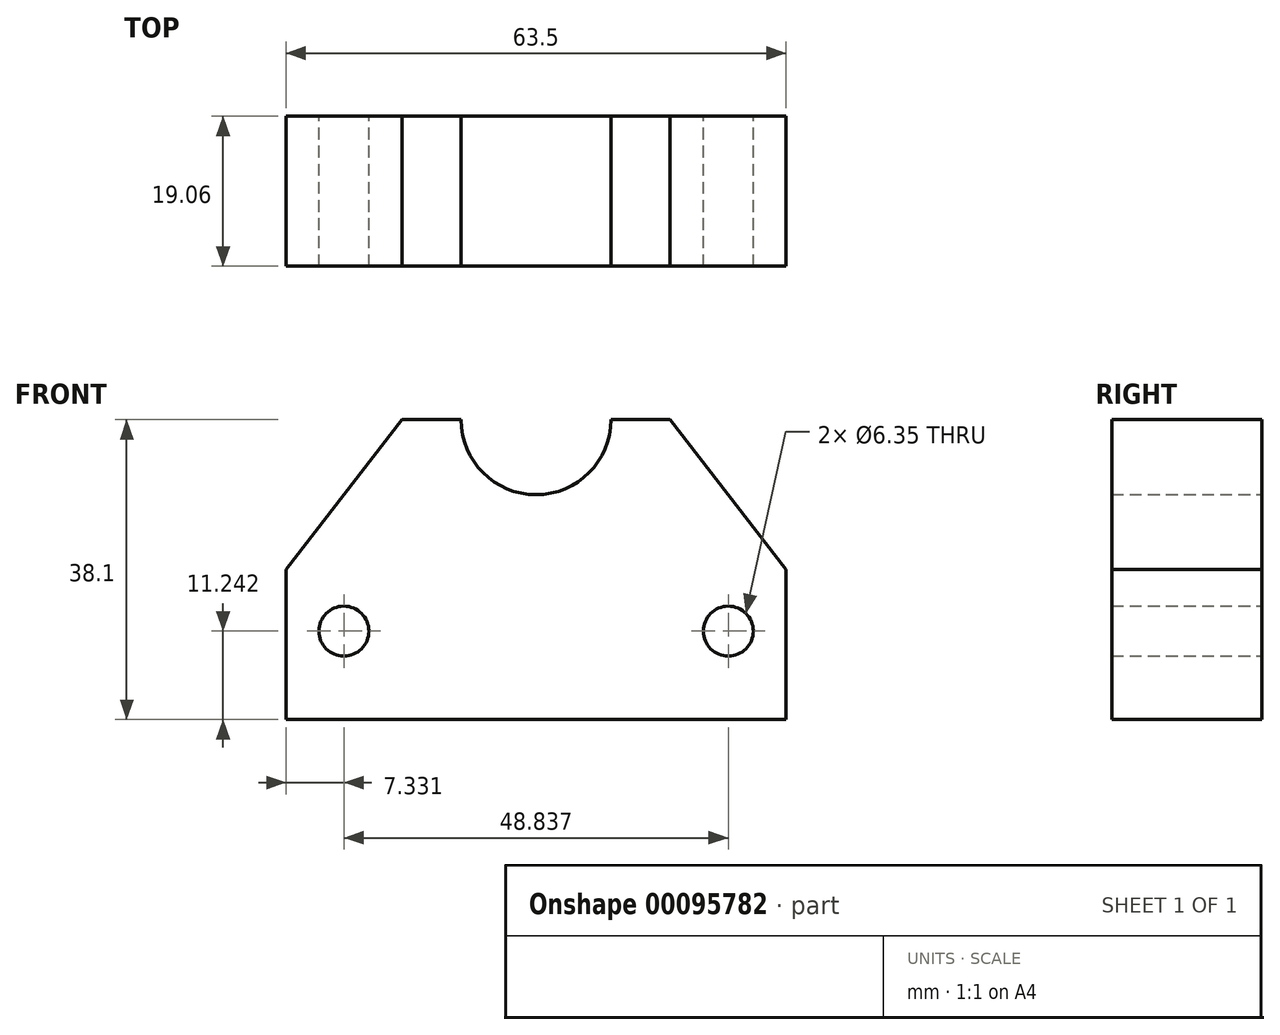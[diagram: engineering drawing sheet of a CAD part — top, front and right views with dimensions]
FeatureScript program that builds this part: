
annotation { "Feature Type Name" : "Feature", "Feature Type Description" : "" }
export const myFeature = defineFeature(function(context is Context, id is Id, definition is map)
    precondition{}
    {
        {
            var Q0;
            Q0=qCreatedBy(makeId("Front.planeOp"),FACE);
            var sketch = newSketch(context, id + "F0", { "sketchPlane" : qUnion([Q0])});
            skLineSegment(sketch, "E0.bottom", {"start": v(-31.75, 19.05) * mm, "end": v(31.75, 19.05) * mm});
            skLineSegment(sketch, "E0.top", {"start": v(-31.75, -19.05) * mm, "end": v(31.75, -19.05) * mm});
            skLineSegment(sketch, "E0.left", {"start": v(-31.75, 19.05) * mm, "end": v(-31.75, -19.05) * mm});
            skLineSegment(sketch, "E0.right", {"start": v(31.75, 19.05) * mm, "end": v(31.75, -19.05) * mm});
            skPoint(sketch, "E0.middle", {"position": v(0, 0) * mm});
            skCircle(sketch, "E1", {"center": v(0, 19.05) * mm, "radius": 9.53 * mm});
            skCircle(sketch, "E2", {"center": v(-24.42, -7.8) * mm, "radius": 3.18 * mm});
            skCircle(sketch, "E3.MirrorC", {"center": v(24.42, -7.8) * mm, "radius": 3.18 * mm});
            skLineSegment(sketch, "E4", {"start": v(-17.04, 19.05) * mm, "end": v(-31.75, 0) * mm});
            skLineSegment(sketch, "E5.MirrorCS", {"start": v(17.04, 19.05) * mm, "end": v(31.75, 0) * mm});
            skSolve(sketch);
        }
        {
            var Q0;
            {var subQ1=sQuery(id+"F0.wireOp",EDGE,"E0.top");Q0=makeQuery(id+"F0.imprint","IMPRINT",FACE,{"disambiguationData":[TD([[makeQuery(id+"F0.imprint","IMPRINT",EDGE,{"derivedFrom":subQ1}),1.0]])]});}
            extrude(context, id + "F1", {"entities" : qUnion([Q0]), "endBound" : BoundingType.SYMMETRIC, "depth" : 19.05 * mm});
        }
        {
            var Q0;
            Q0=makeQuery(id+"F1.opExtrude","SWEPT_BODY",BODY,{"disambiguationData":[OSD([sQuery(id+"F0.wireOp",EDGE,"E0.bottom"),sQuery(id+"F0.wireOp",EDGE,"E0.top"),sQuery(id+"F0.wireOp",EDGE,"E0.left"),sQuery(id+"F0.wireOp",EDGE,"E0.right"),sQuery(id+"F0.wireOp",EDGE,"E1"),sQuery(id+"F0.wireOp",EDGE,"E2"),sQuery(id+"F0.wireOp",EDGE,"E3.MirrorC"),sQuery(id+"F0.wireOp",EDGE,"E4"),sQuery(id+"F0.wireOp",EDGE,"E5.MirrorCS")])]});
            transform(context, id + "F2", {"entities" : qUnion([Q0]), "transformType" : TransformType.TRANSLATION_3D, "dx" : 0 * mm, "dy" : 0 * mm, "dz" : 0 * mm, "makeCopy" : true});
        }
        {
            var Q0;
            Q0=makeQuery(id+"F2.opPattern","COPY",BODY,{"derivedFrom":makeQuery(id+"F1.opExtrude","SWEPT_BODY",BODY,{"disambiguationData":[OSD([sQuery(id+"F0.wireOp",EDGE,"E0.bottom"),sQuery(id+"F0.wireOp",EDGE,"E0.top"),sQuery(id+"F0.wireOp",EDGE,"E0.left"),sQuery(id+"F0.wireOp",EDGE,"E0.right"),sQuery(id+"F0.wireOp",EDGE,"E1"),sQuery(id+"F0.wireOp",EDGE,"E2"),sQuery(id+"F0.wireOp",EDGE,"E3.MirrorC"),sQuery(id+"F0.wireOp",EDGE,"E4"),sQuery(id+"F0.wireOp",EDGE,"E5.MirrorCS")])]}),"instanceName":"1"});
            deleteBodies(context, id + "F3", {"entities" : qUnion([Q0])});
        }
    });
